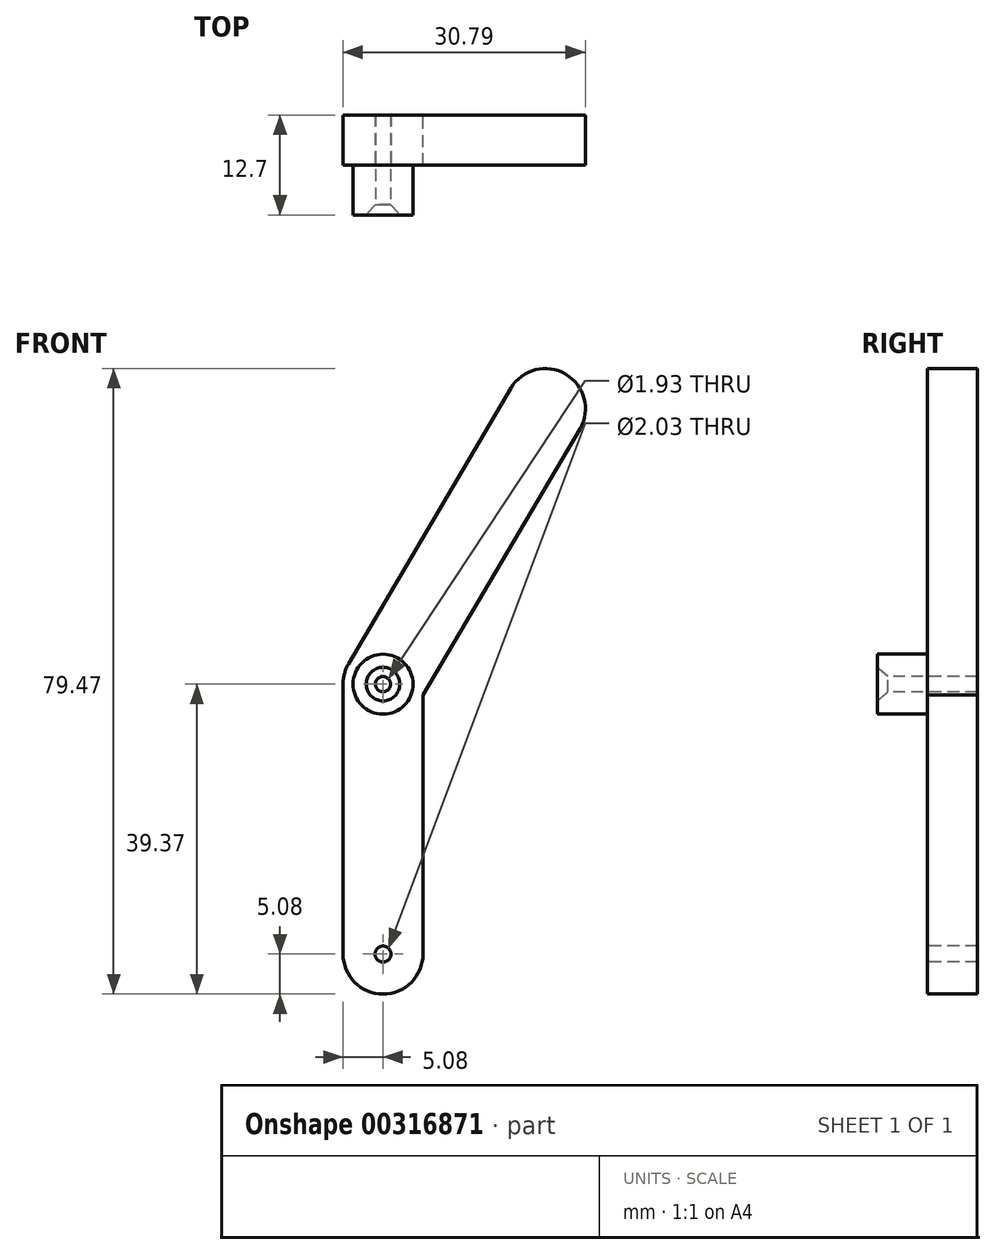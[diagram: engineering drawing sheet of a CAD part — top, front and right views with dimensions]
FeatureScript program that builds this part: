
annotation { "Feature Type Name" : "Feature", "Feature Type Description" : "" }
export const myFeature = defineFeature(function(context is Context, id is Id, definition is map)
    precondition{}
    {
        {
            var Q0;
            Q0=qCreatedBy(makeId("Front.planeOp"),FACE);
            var sketch = newSketch(context, id + "F0", { "sketchPlane" : qUnion([Q0])});
            skLineSegment(sketch, "E0", {"start": v(0, 0) * mm, "end": v(0, 12.7) * mm});
            skLineSegment(sketch, "E1", {"start": v(0, 12.7) * mm, "end": v(0, 34.3) * mm});
            skLineSegment(sketch, "E2", {"start": v(0, 34.3) * mm, "end": v(20.63, 69.3) * mm});
            skArc(sketch, "E3.0.startCap", {"start": v(5.08, 12.7) * mm, "mid": v(0, 7.62) * mm, "end": v(-5.08, 12.7) * mm});
            skArc(sketch, "E3.0.endCap", {"start": v(-5.08, 34.3) * mm, "mid": v(0, 39.37) * mm, "end": v(5.08, 34.3) * mm});
            skLineSegment(sketch, "E3.0.left", {"start": v(-5.08, 12.7) * mm, "end": v(-5.08, 34.3) * mm});
            skLineSegment(sketch, "E3.0.right", {"start": v(5.08, 12.7) * mm, "end": v(5.08, 34.3) * mm});
            skArc(sketch, "E3.1.startCap", {"start": v(5.08, 0) * mm, "mid": v(0, -5.08) * mm, "end": v(-5.08, 0) * mm});
            skArc(sketch, "E3.1.endCap", {"start": v(-5.08, 12.7) * mm, "mid": v(0, 17.78) * mm, "end": v(5.08, 12.7) * mm});
            skLineSegment(sketch, "E3.1.left", {"start": v(-5.08, 0) * mm, "end": v(-5.08, 12.7) * mm});
            skLineSegment(sketch, "E3.1.right", {"start": v(5.08, 0) * mm, "end": v(5.08, 12.7) * mm});
            skArc(sketch, "E3.2.startCap", {"start": v(4.38, 31.71) * mm, "mid": v(-2.58, 29.91) * mm, "end": v(-4.38, 36.87) * mm});
            skArc(sketch, "E3.2.endCap", {"start": v(16.25, 71.88) * mm, "mid": v(23.2, 73.68) * mm, "end": v(25, 66.73) * mm});
            skLineSegment(sketch, "E3.2.left", {"start": v(-4.38, 36.87) * mm, "end": v(16.25, 71.88) * mm});
            skLineSegment(sketch, "E3.2.right", {"start": v(4.38, 31.71) * mm, "end": v(25, 66.73) * mm});
            skSolve(sketch);
        }
        {
            var Q0;
            Q0 = qSketchRegion(id + "F0", true);
            extrude(context, id + "F1", {"entities" : qUnion([Q0]), "depth" : 6.35 * mm});
        }
        {
            var Q0;
            Q0=makeQuery(id+"F1.opExtrude","CAP_FACE",FACE,{"disambiguationData":[OSD([sQuery(id+"F0.wireOp",EDGE,"E3.0.left"),sQuery(id+"F0.wireOp",EDGE,"E3.0.right"),sQuery(id+"F0.wireOp",EDGE,"E3.1.startCap"),sQuery(id+"F0.wireOp",EDGE,"E3.1.left"),sQuery(id+"F0.wireOp",EDGE,"E3.1.right"),sQuery(id+"F0.wireOp",EDGE,"E3.2.startCap"),sQuery(id+"F0.wireOp",EDGE,"E3.2.endCap"),sQuery(id+"F0.wireOp",EDGE,"E3.2.left"),sQuery(id+"F0.wireOp",EDGE,"E3.2.right")])],"isStart":false});
            var sketch = newSketch(context, id + "F2", { "sketchPlane" : qUnion([Q0])});
            skCircle(sketch, "E4", {"center": v(0, 34.3) * mm, "radius": 3.81 * mm});
            skSolve(sketch);
        }
        {
            var Q0;
            Q0=makeQuery(id+"F2.imprint","IMPRINT",FACE,{"disambiguationData":[TD([[makeQuery(id+"F2.imprint","IMPRINT",EDGE,{"derivedFrom":sQuery(id+"F2.wireOp",EDGE,"E4")}),1.0]])]});
            extrude(context, id + "F3", {"entities" : qUnion([Q0]), "operationType" : NewBodyOperationType.ADD, "depth" : 6.35 * mm});
        }
        {
            var Q0;
            Q0=makeQuery(id+"F3.opExtrude","CAP_FACE",FACE,{"disambiguationData":[OSD([sQuery(id+"F2.wireOp",EDGE,"E4")])],"isStart":false});
            var sketch = newSketch(context, id + "F4", { "sketchPlane" : qUnion([Q0])});
            skPoint(sketch, "E5", {"position": v(0, 34.3) * mm});
            skSolve(sketch);
        }
        {
            var Q0;
            Q0=sQuery(id+"F4.wireOp",VERTEX,"E5");
            var Q1;
            Q1=makeQuery(id+"F1.opExtrude","SWEPT_BODY",BODY,{"disambiguationData":[OSD([sQuery(id+"F0.wireOp",EDGE,"E3.0.left"),sQuery(id+"F0.wireOp",EDGE,"E3.0.right"),sQuery(id+"F0.wireOp",EDGE,"E3.1.startCap"),sQuery(id+"F0.wireOp",EDGE,"E3.1.left"),sQuery(id+"F0.wireOp",EDGE,"E3.1.right"),sQuery(id+"F0.wireOp",EDGE,"E3.2.startCap"),sQuery(id+"F0.wireOp",EDGE,"E3.2.endCap"),sQuery(id+"F0.wireOp",EDGE,"E3.2.left"),sQuery(id+"F0.wireOp",EDGE,"E3.2.right")])]});
            hole(context, id + "F5", {"style" : HoleStyle.C_SINK, "endStyle" : HoleEndStyle.THROUGH, "standardTappedOrClearance" : lookupTablePath({ "standard" : "ANSI", "fit" : "Close", "size" : "#1", "type" : "Clearance" }), "standardBlindInLast" : lookupTablePath({ "fit" : "Close", "standard" : "ANSI", "size" : "#1", "type" : "Clearance" }), "holeDiameter" : 1.93 * mm, "cSinkDiameter" : 4.27 * mm, "cSinkAngle" : 82 * degree, "tappedDepth" : 12.7 * mm, "tapClearance" : 3, "locations" : qUnion([Q0]), "scope" : qUnion([Q1])});
        }
        {
            var Q0;
            Q0=makeQuery(id+"F1.opExtrude","CAP_FACE",FACE,{"disambiguationData":[OSD([sQuery(id+"F0.wireOp",EDGE,"E3.0.left"),sQuery(id+"F0.wireOp",EDGE,"E3.0.right"),sQuery(id+"F0.wireOp",EDGE,"E3.1.startCap"),sQuery(id+"F0.wireOp",EDGE,"E3.1.left"),sQuery(id+"F0.wireOp",EDGE,"E3.1.right"),sQuery(id+"F0.wireOp",EDGE,"E3.2.startCap"),sQuery(id+"F0.wireOp",EDGE,"E3.2.endCap"),sQuery(id+"F0.wireOp",EDGE,"E3.2.left"),sQuery(id+"F0.wireOp",EDGE,"E3.2.right")])],"isStart":false});
            var sketch = newSketch(context, id + "F6", { "sketchPlane" : qUnion([Q0])});
            skPoint(sketch, "E6", {"position": v(0, 0) * mm});
            skSolve(sketch);
        }
        {
            var Q0;
            Q0=sQuery(id+"F6.wireOp",VERTEX,"E6");
            var Q1;
            Q1=makeQuery(id+"F1.opExtrude","SWEPT_BODY",BODY,{"disambiguationData":[OSD([sQuery(id+"F0.wireOp",EDGE,"E3.0.left"),sQuery(id+"F0.wireOp",EDGE,"E3.0.right"),sQuery(id+"F0.wireOp",EDGE,"E3.1.startCap"),sQuery(id+"F0.wireOp",EDGE,"E3.1.left"),sQuery(id+"F0.wireOp",EDGE,"E3.1.right"),sQuery(id+"F0.wireOp",EDGE,"E3.2.startCap"),sQuery(id+"F0.wireOp",EDGE,"E3.2.endCap"),sQuery(id+"F0.wireOp",EDGE,"E3.2.left"),sQuery(id+"F0.wireOp",EDGE,"E3.2.right")])]});
            hole(context, id + "F7", {"style" : HoleStyle.SIMPLE, "endStyle" : HoleEndStyle.THROUGH, "holeDiameter" : 2.03 * mm, "tappedDepth" : 12.7 * mm, "tapClearance" : 3, "locations" : qUnion([Q0]), "scope" : qUnion([Q1])});
        }
    });
